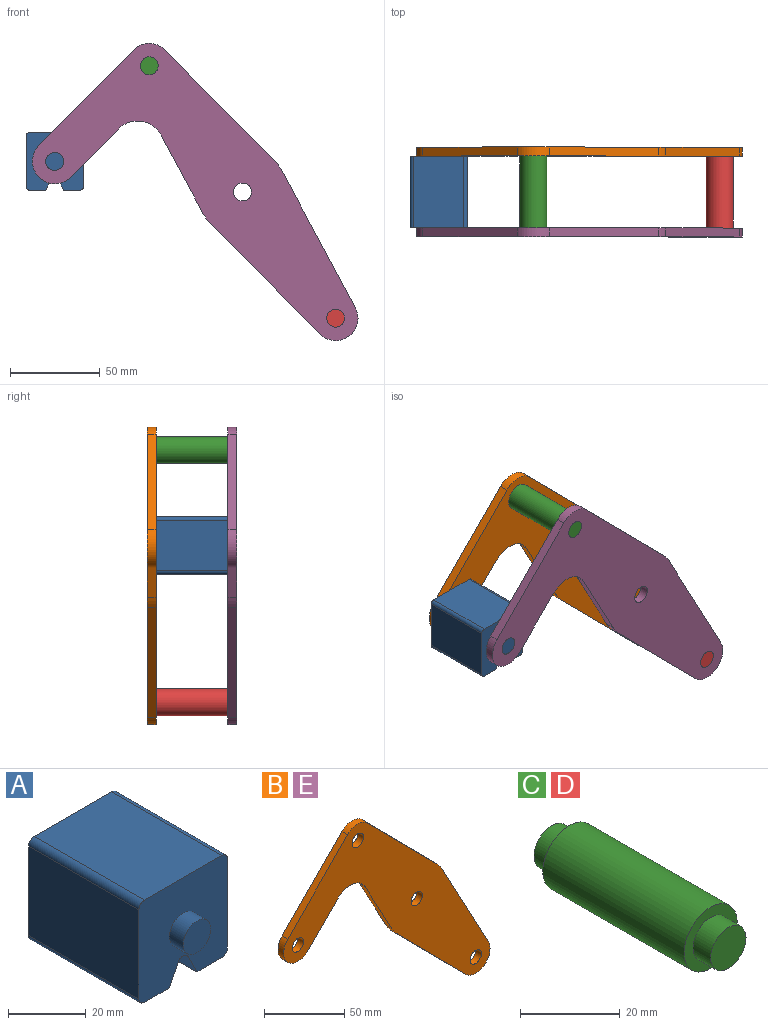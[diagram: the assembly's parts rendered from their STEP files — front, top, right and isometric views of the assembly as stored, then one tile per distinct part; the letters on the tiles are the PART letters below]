
ASSEMBLY  parts=5 mates=3
PART A: 18 faces, bbox 32.1x50x32.1 mm
  f0: plane 40x28.08mm, normal (1,0,0), area 1123.1mm2, adj f4,f10,f13,f14
  f1: plane 40x9.04mm, normal (0,0,-1), area 361.6mm2, adj f2,f4,f10,f14
  f2: plane 40x6.42mm, normal (-0.89,0,-0.45), area 287.2mm2, adj f1,f4,f10,f15
  f3: plane 40x6.42mm, normal (0.89,0,-0.45), area 287.2mm2, adj f4,f5,f10,f15
  f4: plane 32.08x32.08mm, normal (0,-1,0), area 900.6mm2, adj f0,f1,f2,f3,f5,f6,f7,f9
  f5: plane 40x9.04mm, normal (0,0,-1), area 361.6mm2, adj f3,f4,f10,f16
  f6: plane 40x28.08mm, normal (0,0,1), area 1123.1mm2, adj f4,f10,f13,f17
  f7: plane 40x28.08mm, normal (-1,0,0), area 1123.1mm2, adj f4,f10,f16,f17
  f8: plane 10x10mm, normal (0,-1,0), area 78.5mm2, adj f9
  f9: cylinder r=5mm len=10mm, axis (0,1,0), area 157.1mm2, adj f4,f8
  f10: plane 32.08x32.08mm, normal (0,1,0), area 900.6mm2, adj f0,f1,f2,f3,f5,f6,f7,f12
  f11: plane 10x10mm, normal (0,1,0), area 78.5mm2, adj f12
  f12: cylinder r=5mm len=10mm, axis (0,-1,0), area 157.1mm2, adj f10,f11
  f13: cylinder r=2mm len=40mm, axis (0,1,0), area 125.7mm2, adj f0,f4,f6,f10
  f14: cylinder r=2mm len=40mm, axis (0,-1,0), area 125.7mm2, adj f0,f1,f4,f10
  f15: cylinder r=2mm len=40mm, axis (0,1,0), area 177.1mm2, adj f2,f3,f4,f10
  f16: cylinder r=2mm len=40mm, axis (0,1,0), area 125.7mm2, adj f4,f5,f7,f10
  f17: cylinder r=2mm len=40mm, axis (0,-1,0), area 125.7mm2, adj f4,f6,f7,f10
PART B: 18 faces, bbox 181.7x5x165.8 mm
  f0: plane 43.49x23.35mm, normal (-0.88,0,-0.47), area 246.8mm2, adj f1,f14,f16,f17
  f1: cylinder r=25mm len=5.75mm, axis (0,1,0), area 35.8mm2, adj f0,f2,f16,f17
  f2: plane 61.6x60.87mm, normal (-0.71,0,-0.7), area 433mm2, adj f1,f3,f16,f17
  f3: cylinder r=12.5mm len=21.39mm, axis (0,1,0), area 178.4mm2, adj f2,f4,f16,f17
  f4: plane 76.3x40.96mm, normal (0.88,0,0.47), area 433mm2, adj f3,f5,f16,f17
  f5: cylinder r=25mm len=5.75mm, axis (0,1,0), area 35.8mm2, adj f4,f6,f16,f17
  f6: plane 61.6x60.87mm, normal (0.71,0,0.7), area 433mm2, adj f5,f7,f16,f17
  f7: cylinder r=12.5mm len=17.78mm, axis (0,1,0), area 98.9mm2, adj f6,f8,f16,f17
  f8: plane 53.35x52.71mm, normal (-0.71,0,0.7), area 375mm2, adj f7,f9,f16,f17
  f9: cylinder r=12.5mm len=21.39mm, axis (0,1,0), area 196.3mm2, adj f8,f10,f16,f17
  f10: plane 26.86x26.54mm, normal (0.71,0,-0.7), area 188.8mm2, adj f9,f14,f16,f17
  f11: cylinder r=5mm len=10mm, axis (0,1,0), area 157.1mm2, adj f16,f17
  f12: cylinder r=5mm len=10mm, axis (0,1,0), area 157.1mm2, adj f16,f17
  f13: cylinder r=5mm len=10mm, axis (0,1,0), area 157.1mm2, adj f16,f17
  f14: cylinder r=15mm len=23.89mm, axis (0,1,0), area 140.2mm2, adj f0,f10,f16,f17
  f15: cylinder r=5mm len=10mm, axis (0,1,0), area 157.1mm2, adj f16,f17
  f16: plane 181.66x165.78mm, normal (0,-1,0), area 8710.1mm2, adj f0,f1,f2,f3,f4,f5,f6,f7
  f17: plane 181.66x165.78mm, normal (0,1,0), area 8710.1mm2, adj f0,f1,f2,f3,f4,f5,f6,f7
PART C: 7 faces, bbox 15x50x15 mm
  f0: cylinder r=7.5mm len=40mm, axis (0,-1,0), area 1885mm2, adj f2,f5
  f1: cylinder r=5mm len=10mm, axis (0,1,0), area 157.1mm2, adj f2,f3
  f2: plane 15x15mm, normal (0,-1,0), area 98.2mm2, adj f0,f1
  f3: plane 10x10mm, normal (0,-1,0), area 78.5mm2, adj f1
  f4: cylinder r=5mm len=10mm, axis (0,-1,0), area 157.1mm2, adj f5,f6
  f5: plane 15x15mm, normal (0,1,0), area 98.2mm2, adj f0,f4
  f6: plane 10x10mm, normal (0,1,0), area 78.5mm2, adj f4
PART D: same geometry as C
PART E: same geometry as B
PLACE A t=(0,-20,0)mm
PLACE B t=(0,25,0)mm
PLACE C t=(0,-20,0)mm
PLACE D t=(103.95,-20,-140.78)mm
PLACE E t=(0,-20,0)mm fixed
MATE revolute E.f9 <-> A.f9  axis (0,1,0) through (-104.69,-20,17.04)mm
MATE fastened D.f0 <-> E.f3  axis (0,-1,0) through (51.98,-20,-70.39)mm
MATE fastened C.f0 <-> B.f7  axis (0,1,0) through (-51.98,20,70.39)mm
